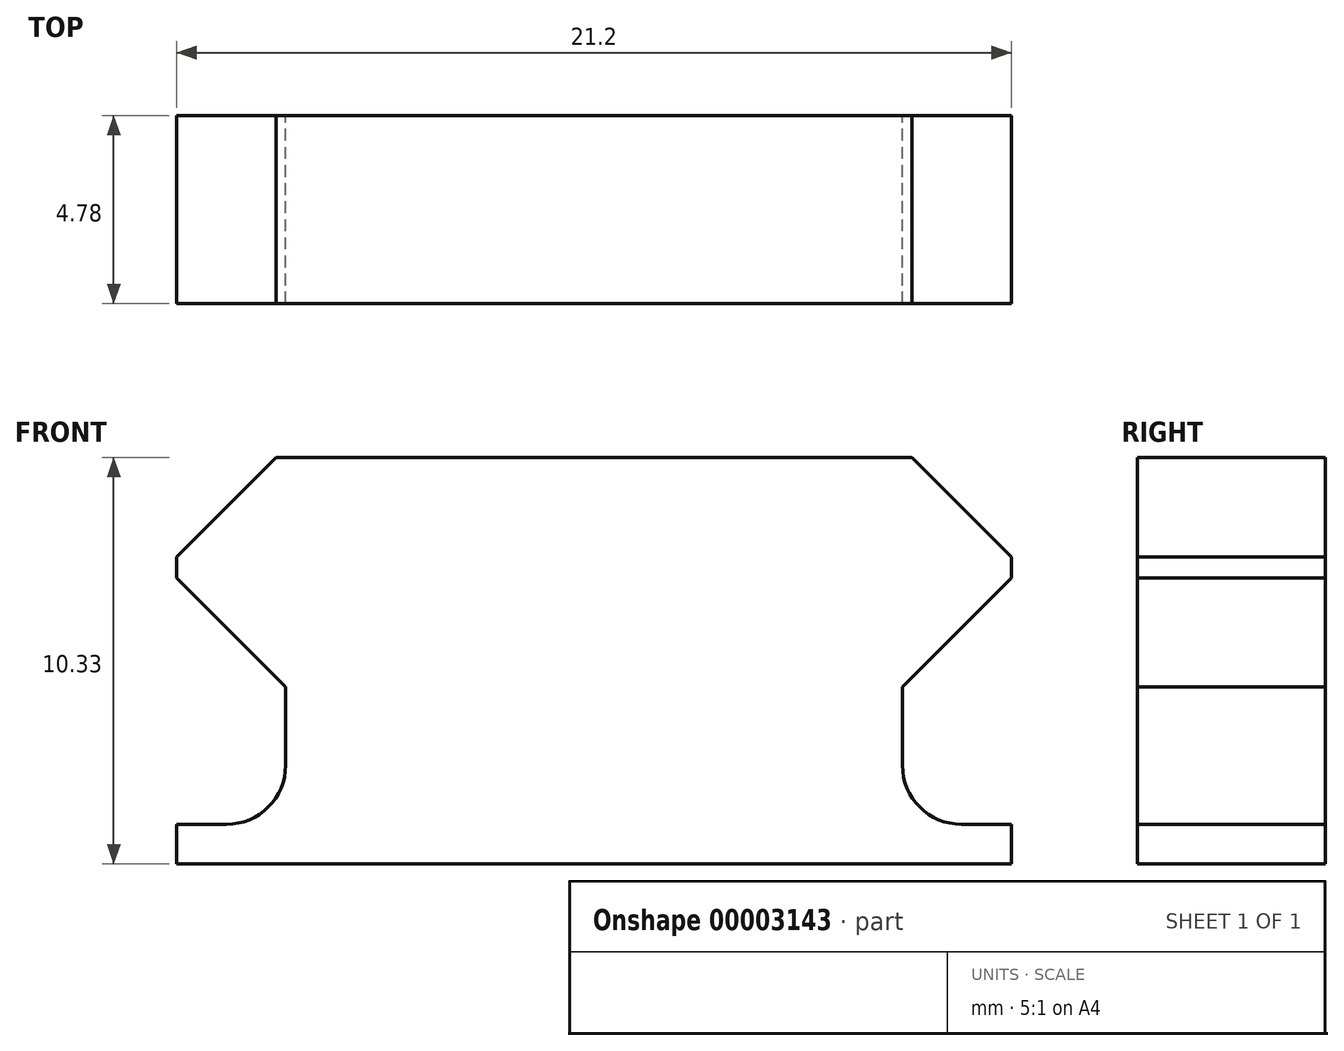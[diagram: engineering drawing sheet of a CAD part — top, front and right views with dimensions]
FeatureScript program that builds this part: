
annotation { "Feature Type Name" : "Feature", "Feature Type Description" : "" }
export const myFeature = defineFeature(function(context is Context, id is Id, definition is map)
    precondition{}
    {
        {
            var Q0;
            Q0=qCreatedBy(makeId("Front.planeOp"),FACE);
            var sketch = newSketch(context, id + "F0", { "sketchPlane" : qUnion([Q0])});
            skLineSegment(sketch, "E0", {"start": v(0, 15.8) * mm, "end": v(0, -17.85) * mm, "construction": true});
            skLineSegment(sketch, "E1", {"start": v(-10.6, -4.36) * mm, "end": v(0, -4.36) * mm});
            skLineSegment(sketch, "E2.0.MirrorCS", {"start": v(10.6, -4.36) * mm, "end": v(0, -4.36) * mm});
            skLineSegment(sketch, "E3", {"start": v(-10.6, -4.36) * mm, "end": v(-10.6, -3.36) * mm});
            skLineSegment(sketch, "E4", {"start": v(-10.6, -3.36) * mm, "end": v(-9.34, -3.36) * mm});
            skLineSegment(sketch, "E5", {"start": v(10.6, -4.36) * mm, "end": v(10.6, -3.36) * mm});
            skLineSegment(sketch, "E6", {"start": v(10.6, -3.36) * mm, "end": v(9.34, -3.36) * mm});
            skLineSegment(sketch, "E7", {"start": v(-7.84, -1.86) * mm, "end": v(-7.84, 5.97) * mm});
            skLineSegment(sketch, "E8.0.MirrorCS", {"start": v(7.84, -1.86) * mm, "end": v(7.84, 5.97) * mm});
            skLineSegment(sketch, "E9", {"start": v(-10.6, -8.18) * mm, "end": v(-10.6, 7.36) * mm, "construction": true});
            skPoint(sketch, "E10.newPointA", {"position": v(7.84, -3.36) * mm});
            skArc(sketch, "E10.filletArc", {"start": v(7.84, -1.86) * mm, "mid": v(8.27, -2.92) * mm, "end": v(9.34, -3.36) * mm});
            skPoint(sketch, "E11.newPointA", {"position": v(-7.84, -3.36) * mm});
            skPoint(sketch, "E11.newPointB", {"position": v(0, -3.36) * mm});
            skArc(sketch, "E11.filletArc", {"start": v(-9.34, -3.36) * mm, "mid": v(-8.27, -2.92) * mm, "end": v(-7.84, -1.86) * mm});
            skLineSegment(sketch, "E12", {"start": v(-11.77, 5.97) * mm, "end": v(12.47, 5.97) * mm, "construction": true});
            skLineSegment(sketch, "E13", {"start": v(9.5, 5.97) * mm, "end": v(9.5, 1.8) * mm, "construction": true});
            skLineSegment(sketch, "E14", {"start": v(9.5, 1.8) * mm, "end": v(-12.15, 1.8) * mm, "construction": true});
            skLineSegment(sketch, "E15", {"start": v(-12.35, 4.54) * mm, "end": v(10.6, 4.54) * mm, "construction": true});
            skLineSegment(sketch, "E16", {"start": v(10.6, -4.36) * mm, "end": v(10.6, 9.86) * mm, "construction": true});
            skLineSegment(sketch, "E17.0.MirrorCS", {"start": v(-9.5, 5.97) * mm, "end": v(-9.5, 1.8) * mm, "construction": true});
            skLineSegment(sketch, "E18", {"start": v(9.5, 4.54) * mm, "end": v(10.6, 3.44) * mm});
            skLineSegment(sketch, "E19", {"start": v(9.5, 1.8) * mm, "end": v(10.6, 2.9) * mm});
            skLineSegment(sketch, "E20", {"start": v(10.6, 3.44) * mm, "end": v(10.6, 2.9) * mm});
            skLineSegment(sketch, "E21", {"start": v(9.5, 4.54) * mm, "end": v(8.08, 5.97) * mm});
            skLineSegment(sketch, "E22", {"start": v(8.08, 5.97) * mm, "end": v(-7.84, 5.97) * mm});
            skLineSegment(sketch, "E23", {"start": v(10.6, 2.9) * mm, "end": v(7.84, 0.14) * mm});
            skLineSegment(sketch, "E24.0.MirrorCS", {"start": v(-10.6, 2.9) * mm, "end": v(-7.84, 0.14) * mm});
            skLineSegment(sketch, "E25.0.MirrorCS", {"start": v(-9.5, 4.54) * mm, "end": v(-10.6, 3.44) * mm});
            skLineSegment(sketch, "E26.0.MirrorCS", {"start": v(-9.5, 4.54) * mm, "end": v(-8.08, 5.97) * mm});
            skLineSegment(sketch, "E27.0.MirrorCS", {"start": v(-10.6, 3.44) * mm, "end": v(-10.6, 2.9) * mm});
            skLineSegment(sketch, "E28", {"start": v(-8.08, 5.97) * mm, "end": v(-7.84, 5.97) * mm});
            skLineSegment(sketch, "E29", {"start": v(7.84, 0.14) * mm, "end": v(-7.84, 0.14) * mm});
            skSolve(sketch);
        }
        {
            var Q0;
            Q0=qSketchRegion(id+"F0",true);
            extrude(context, id + "F1", {"entities" : qUnion([Q0]), "depth" : 4.78 * mm});
        }
    });
